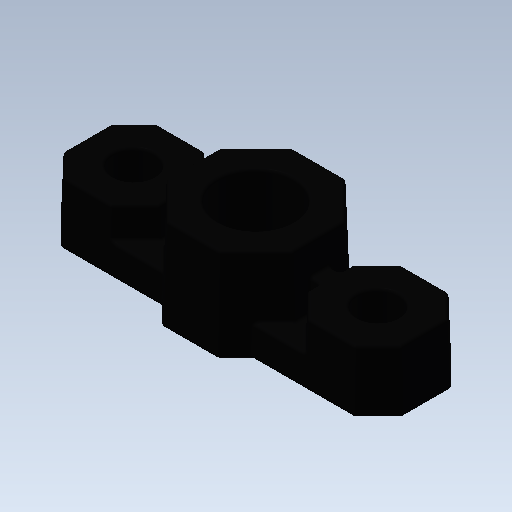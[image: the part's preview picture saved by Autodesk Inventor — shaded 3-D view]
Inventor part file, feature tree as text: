
AUTODESK INVENTOR PART (.ipt)
format: ipt  version: 2020 (Build 240168000, 168)  size: 751,104 bytes
history: native  units: in
note: dims shown in document units (in); Inventor stores cm internally (conversion verified against a paired STEP export)
features: other x1, fillet x1, imported_body x1
ambient origin geometry x8: Origin, YZ Plane, XZ Plane, XY Plane, X Axis, Y Axis, Z Axis, Center Point
bodies: Body1 (feature_tree)
feature tree (3):
  other  "Bearing Block HS"
  fillet  "Fillet7"  [1 undecoded]
  imported_body  "Base1"
note: 1 required parameter value undecoded (feature->parameter linkage not recoverable at this tier; creation-order binding heuristic only, values carry confidence <= 0.55)
